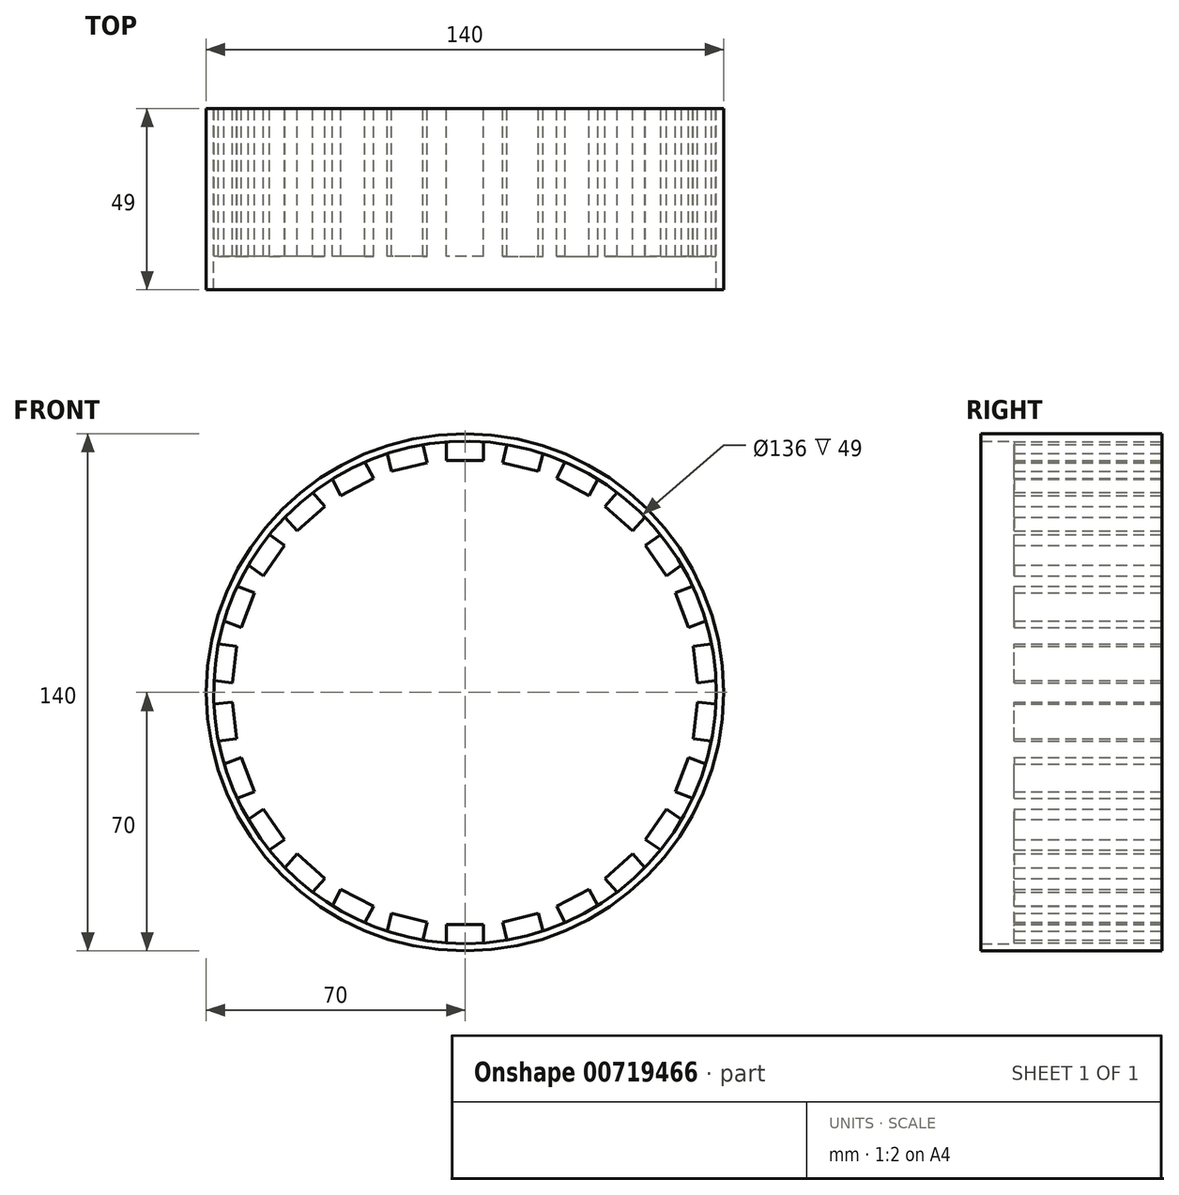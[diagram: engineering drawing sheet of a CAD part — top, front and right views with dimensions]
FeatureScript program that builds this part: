
annotation { "Feature Type Name" : "Feature", "Feature Type Description" : "" }
export const myFeature = defineFeature(function(context is Context, id is Id, definition is map)
    precondition{}
    {
        {
            var Q0;
            Q0=qCreatedBy(makeId("Front.planeOp"),FACE);
            var sketch = newSketch(context, id + "F0", { "sketchPlane" : qUnion([Q0])});
            skCircle(sketch, "E0", {"center": v(0, 0) * mm, "radius": 68 * mm});
            skCircle(sketch, "E1", {"center": v(0, 0) * mm, "radius": 70 * mm});
            skLineSegment(sketch, "E2", {"start": v(5, 67.82) * mm, "end": v(5, 62.82) * mm});
            skLineSegment(sketch, "E3", {"start": v(5, 62.82) * mm, "end": v(-5, 62.82) * mm});
            skLineSegment(sketch, "E4", {"start": v(-5, 62.82) * mm, "end": v(-5, 67.82) * mm});
            skSolve(sketch);
        }
        {
            var Q0;
            {var subQ0=sQuery(id+"F0.wireOp",EDGE,"E2");Q0=makeQuery(id+"F0.imprint","IMPRINT",FACE,{"disambiguationData":[TD([[makeQuery(id+"F0.imprint","IMPRINT",EDGE,{"derivedFrom":subQ0}),-1.0]])]});}
            var Q1;
            Q1=makeQuery(id+"F0.imprint","IMPRINT",FACE,{"disambiguationData":[TD([[makeQuery(id+"F0.imprint","IMPRINT",EDGE,{"derivedFrom":sQuery(id+"F0.wireOp",EDGE,"E1")}),1.0]])]});
            extrude(context, id + "F1", {"entities" : qUnion([Q0, Q1]), "depth" : 40 * mm, "offsetDistance" : 25 * mm});
        }
        {
            var Q0;
            Q0=makeQuery(id+"F1.opExtrude","SWEPT_BODY",BODY,{"disambiguationData":[OSD([sQuery(id+"F0.wireOp",EDGE,"E0"),sQuery(id+"F0.wireOp",EDGE,"E1"),sQuery(id+"F0.wireOp",EDGE,"E2"),sQuery(id+"F0.wireOp",EDGE,"E3"),sQuery(id+"F0.wireOp",EDGE,"E4")])]});
            var Q1;
            Q1=makeQuery(id+"F1.opExtrude","SWEPT_FACE",FACE,{"disambiguationData":[OSD([sQuery(id+"F0.wireOp",EDGE,"E0")])]});
            circularPattern(context, id + "F2", {"entities" : qUnion([Q0]), "axis" : qUnion([Q1]), "angle" : 360 * degree, "instanceCount" : 26, "equalSpace" : true});
        }
        {
            var Q0;
            Q0=makeQuery(id+"F2.opPattern","COPY",BODY,{"derivedFrom":makeQuery(id+"F1.opExtrude","SWEPT_BODY",BODY,{"disambiguationData":[OSD([sQuery(id+"F0.wireOp",EDGE,"E0"),sQuery(id+"F0.wireOp",EDGE,"E1"),sQuery(id+"F0.wireOp",EDGE,"E2"),sQuery(id+"F0.wireOp",EDGE,"E3"),sQuery(id+"F0.wireOp",EDGE,"E4")])]}),"instanceName":"3"});
            var Q1;
            Q1=makeQuery(id+"F2.opPattern","COPY",BODY,{"derivedFrom":makeQuery(id+"F1.opExtrude","SWEPT_BODY",BODY,{"disambiguationData":[OSD([sQuery(id+"F0.wireOp",EDGE,"E0"),sQuery(id+"F0.wireOp",EDGE,"E1"),sQuery(id+"F0.wireOp",EDGE,"E2"),sQuery(id+"F0.wireOp",EDGE,"E3"),sQuery(id+"F0.wireOp",EDGE,"E4")])]}),"instanceName":"4"});
            var Q2;
            Q2=makeQuery(id+"F2.opPattern","COPY",BODY,{"derivedFrom":makeQuery(id+"F1.opExtrude","SWEPT_BODY",BODY,{"disambiguationData":[OSD([sQuery(id+"F0.wireOp",EDGE,"E0"),sQuery(id+"F0.wireOp",EDGE,"E1"),sQuery(id+"F0.wireOp",EDGE,"E2"),sQuery(id+"F0.wireOp",EDGE,"E3"),sQuery(id+"F0.wireOp",EDGE,"E4")])]}),"instanceName":"6"});
            var Q3;
            Q3=makeQuery(id+"F2.opPattern","COPY",BODY,{"derivedFrom":makeQuery(id+"F1.opExtrude","SWEPT_BODY",BODY,{"disambiguationData":[OSD([sQuery(id+"F0.wireOp",EDGE,"E0"),sQuery(id+"F0.wireOp",EDGE,"E1"),sQuery(id+"F0.wireOp",EDGE,"E2"),sQuery(id+"F0.wireOp",EDGE,"E3"),sQuery(id+"F0.wireOp",EDGE,"E4")])]}),"instanceName":"10"});
            var Q4;
            Q4=makeQuery(id+"F2.opPattern","COPY",BODY,{"derivedFrom":makeQuery(id+"F1.opExtrude","SWEPT_BODY",BODY,{"disambiguationData":[OSD([sQuery(id+"F0.wireOp",EDGE,"E0"),sQuery(id+"F0.wireOp",EDGE,"E1"),sQuery(id+"F0.wireOp",EDGE,"E2"),sQuery(id+"F0.wireOp",EDGE,"E3"),sQuery(id+"F0.wireOp",EDGE,"E4")])]}),"instanceName":"8"});
            var Q5;
            Q5=makeQuery(id+"F2.opPattern","COPY",BODY,{"derivedFrom":makeQuery(id+"F1.opExtrude","SWEPT_BODY",BODY,{"disambiguationData":[OSD([sQuery(id+"F0.wireOp",EDGE,"E0"),sQuery(id+"F0.wireOp",EDGE,"E1"),sQuery(id+"F0.wireOp",EDGE,"E2"),sQuery(id+"F0.wireOp",EDGE,"E3"),sQuery(id+"F0.wireOp",EDGE,"E4")])]}),"instanceName":"11"});
            var Q6;
            Q6=makeQuery(id+"F2.opPattern","COPY",BODY,{"derivedFrom":makeQuery(id+"F1.opExtrude","SWEPT_BODY",BODY,{"disambiguationData":[OSD([sQuery(id+"F0.wireOp",EDGE,"E0"),sQuery(id+"F0.wireOp",EDGE,"E1"),sQuery(id+"F0.wireOp",EDGE,"E2"),sQuery(id+"F0.wireOp",EDGE,"E3"),sQuery(id+"F0.wireOp",EDGE,"E4")])]}),"instanceName":"12"});
            var Q7;
            Q7=makeQuery(id+"F2.opPattern","COPY",BODY,{"derivedFrom":makeQuery(id+"F1.opExtrude","SWEPT_BODY",BODY,{"disambiguationData":[OSD([sQuery(id+"F0.wireOp",EDGE,"E0"),sQuery(id+"F0.wireOp",EDGE,"E1"),sQuery(id+"F0.wireOp",EDGE,"E2"),sQuery(id+"F0.wireOp",EDGE,"E3"),sQuery(id+"F0.wireOp",EDGE,"E4")])]}),"instanceName":"9"});
            var Q8;
            Q8=makeQuery(id+"F2.opPattern","COPY",BODY,{"derivedFrom":makeQuery(id+"F1.opExtrude","SWEPT_BODY",BODY,{"disambiguationData":[OSD([sQuery(id+"F0.wireOp",EDGE,"E0"),sQuery(id+"F0.wireOp",EDGE,"E1"),sQuery(id+"F0.wireOp",EDGE,"E2"),sQuery(id+"F0.wireOp",EDGE,"E3"),sQuery(id+"F0.wireOp",EDGE,"E4")])]}),"instanceName":"2"});
            var Q9;
            Q9=makeQuery(id+"F2.opPattern","COPY",BODY,{"derivedFrom":makeQuery(id+"F1.opExtrude","SWEPT_BODY",BODY,{"disambiguationData":[OSD([sQuery(id+"F0.wireOp",EDGE,"E0"),sQuery(id+"F0.wireOp",EDGE,"E1"),sQuery(id+"F0.wireOp",EDGE,"E2"),sQuery(id+"F0.wireOp",EDGE,"E3"),sQuery(id+"F0.wireOp",EDGE,"E4")])]}),"instanceName":"15"});
            var Q10;
            Q10=makeQuery(id+"F2.opPattern","COPY",BODY,{"derivedFrom":makeQuery(id+"F1.opExtrude","SWEPT_BODY",BODY,{"disambiguationData":[OSD([sQuery(id+"F0.wireOp",EDGE,"E0"),sQuery(id+"F0.wireOp",EDGE,"E1"),sQuery(id+"F0.wireOp",EDGE,"E2"),sQuery(id+"F0.wireOp",EDGE,"E3"),sQuery(id+"F0.wireOp",EDGE,"E4")])]}),"instanceName":"13"});
            var Q11;
            Q11=makeQuery(id+"F2.opPattern","COPY",BODY,{"derivedFrom":makeQuery(id+"F1.opExtrude","SWEPT_BODY",BODY,{"disambiguationData":[OSD([sQuery(id+"F0.wireOp",EDGE,"E0"),sQuery(id+"F0.wireOp",EDGE,"E1"),sQuery(id+"F0.wireOp",EDGE,"E2"),sQuery(id+"F0.wireOp",EDGE,"E3"),sQuery(id+"F0.wireOp",EDGE,"E4")])]}),"instanceName":"16"});
            var Q12;
            Q12=makeQuery(id+"F2.opPattern","COPY",BODY,{"derivedFrom":makeQuery(id+"F1.opExtrude","SWEPT_BODY",BODY,{"disambiguationData":[OSD([sQuery(id+"F0.wireOp",EDGE,"E0"),sQuery(id+"F0.wireOp",EDGE,"E1"),sQuery(id+"F0.wireOp",EDGE,"E2"),sQuery(id+"F0.wireOp",EDGE,"E3"),sQuery(id+"F0.wireOp",EDGE,"E4")])]}),"instanceName":"14"});
            var Q13;
            Q13=makeQuery(id+"F2.opPattern","COPY",BODY,{"derivedFrom":makeQuery(id+"F1.opExtrude","SWEPT_BODY",BODY,{"disambiguationData":[OSD([sQuery(id+"F0.wireOp",EDGE,"E0"),sQuery(id+"F0.wireOp",EDGE,"E1"),sQuery(id+"F0.wireOp",EDGE,"E2"),sQuery(id+"F0.wireOp",EDGE,"E3"),sQuery(id+"F0.wireOp",EDGE,"E4")])]}),"instanceName":"19"});
            var Q14;
            Q14=makeQuery(id+"F2.opPattern","COPY",BODY,{"derivedFrom":makeQuery(id+"F1.opExtrude","SWEPT_BODY",BODY,{"disambiguationData":[OSD([sQuery(id+"F0.wireOp",EDGE,"E0"),sQuery(id+"F0.wireOp",EDGE,"E1"),sQuery(id+"F0.wireOp",EDGE,"E2"),sQuery(id+"F0.wireOp",EDGE,"E3"),sQuery(id+"F0.wireOp",EDGE,"E4")])]}),"instanceName":"18"});
            var Q15;
            Q15=makeQuery(id+"F2.opPattern","COPY",BODY,{"derivedFrom":makeQuery(id+"F1.opExtrude","SWEPT_BODY",BODY,{"disambiguationData":[OSD([sQuery(id+"F0.wireOp",EDGE,"E0"),sQuery(id+"F0.wireOp",EDGE,"E1"),sQuery(id+"F0.wireOp",EDGE,"E2"),sQuery(id+"F0.wireOp",EDGE,"E3"),sQuery(id+"F0.wireOp",EDGE,"E4")])]}),"instanceName":"17"});
            var Q16;
            Q16=makeQuery(id+"F2.opPattern","COPY",BODY,{"derivedFrom":makeQuery(id+"F1.opExtrude","SWEPT_BODY",BODY,{"disambiguationData":[OSD([sQuery(id+"F0.wireOp",EDGE,"E0"),sQuery(id+"F0.wireOp",EDGE,"E1"),sQuery(id+"F0.wireOp",EDGE,"E2"),sQuery(id+"F0.wireOp",EDGE,"E3"),sQuery(id+"F0.wireOp",EDGE,"E4")])]}),"instanceName":"7"});
            var Q17;
            Q17=makeQuery(id+"F2.opPattern","COPY",BODY,{"derivedFrom":makeQuery(id+"F1.opExtrude","SWEPT_BODY",BODY,{"disambiguationData":[OSD([sQuery(id+"F0.wireOp",EDGE,"E0"),sQuery(id+"F0.wireOp",EDGE,"E1"),sQuery(id+"F0.wireOp",EDGE,"E2"),sQuery(id+"F0.wireOp",EDGE,"E3"),sQuery(id+"F0.wireOp",EDGE,"E4")])]}),"instanceName":"23"});
            var Q18;
            Q18=makeQuery(id+"F2.opPattern","COPY",BODY,{"derivedFrom":makeQuery(id+"F1.opExtrude","SWEPT_BODY",BODY,{"disambiguationData":[OSD([sQuery(id+"F0.wireOp",EDGE,"E0"),sQuery(id+"F0.wireOp",EDGE,"E1"),sQuery(id+"F0.wireOp",EDGE,"E2"),sQuery(id+"F0.wireOp",EDGE,"E3"),sQuery(id+"F0.wireOp",EDGE,"E4")])]}),"instanceName":"22"});
            var Q19;
            Q19=makeQuery(id+"F2.opPattern","COPY",BODY,{"derivedFrom":makeQuery(id+"F1.opExtrude","SWEPT_BODY",BODY,{"disambiguationData":[OSD([sQuery(id+"F0.wireOp",EDGE,"E0"),sQuery(id+"F0.wireOp",EDGE,"E1"),sQuery(id+"F0.wireOp",EDGE,"E2"),sQuery(id+"F0.wireOp",EDGE,"E3"),sQuery(id+"F0.wireOp",EDGE,"E4")])]}),"instanceName":"21"});
            var Q20;
            Q20=makeQuery(id+"F2.opPattern","COPY",BODY,{"derivedFrom":makeQuery(id+"F1.opExtrude","SWEPT_BODY",BODY,{"disambiguationData":[OSD([sQuery(id+"F0.wireOp",EDGE,"E0"),sQuery(id+"F0.wireOp",EDGE,"E1"),sQuery(id+"F0.wireOp",EDGE,"E2"),sQuery(id+"F0.wireOp",EDGE,"E3"),sQuery(id+"F0.wireOp",EDGE,"E4")])]}),"instanceName":"20"});
            var Q21;
            Q21=makeQuery(id+"F2.opPattern","COPY",BODY,{"derivedFrom":makeQuery(id+"F1.opExtrude","SWEPT_BODY",BODY,{"disambiguationData":[OSD([sQuery(id+"F0.wireOp",EDGE,"E0"),sQuery(id+"F0.wireOp",EDGE,"E1"),sQuery(id+"F0.wireOp",EDGE,"E2"),sQuery(id+"F0.wireOp",EDGE,"E3"),sQuery(id+"F0.wireOp",EDGE,"E4")])]}),"instanceName":"24"});
            var Q22;
            Q22=makeQuery(id+"F2.opPattern","COPY",BODY,{"derivedFrom":makeQuery(id+"F1.opExtrude","SWEPT_BODY",BODY,{"disambiguationData":[OSD([sQuery(id+"F0.wireOp",EDGE,"E0"),sQuery(id+"F0.wireOp",EDGE,"E1"),sQuery(id+"F0.wireOp",EDGE,"E2"),sQuery(id+"F0.wireOp",EDGE,"E3"),sQuery(id+"F0.wireOp",EDGE,"E4")])]}),"instanceName":"1"});
            var Q23;
            Q23=makeQuery(id+"F1.opExtrude","SWEPT_BODY",BODY,{"disambiguationData":[OSD([sQuery(id+"F0.wireOp",EDGE,"E0"),sQuery(id+"F0.wireOp",EDGE,"E1"),sQuery(id+"F0.wireOp",EDGE,"E2"),sQuery(id+"F0.wireOp",EDGE,"E3"),sQuery(id+"F0.wireOp",EDGE,"E4")])]});
            var Q24;
            Q24=makeQuery(id+"F2.opPattern","COPY",BODY,{"derivedFrom":makeQuery(id+"F1.opExtrude","SWEPT_BODY",BODY,{"disambiguationData":[OSD([sQuery(id+"F0.wireOp",EDGE,"E0"),sQuery(id+"F0.wireOp",EDGE,"E1"),sQuery(id+"F0.wireOp",EDGE,"E2"),sQuery(id+"F0.wireOp",EDGE,"E3"),sQuery(id+"F0.wireOp",EDGE,"E4")])]}),"instanceName":"25"});
            var Q25;
            Q25=makeQuery(id+"F2.opPattern","COPY",BODY,{"derivedFrom":makeQuery(id+"F1.opExtrude","SWEPT_BODY",BODY,{"disambiguationData":[OSD([sQuery(id+"F0.wireOp",EDGE,"E0"),sQuery(id+"F0.wireOp",EDGE,"E1"),sQuery(id+"F0.wireOp",EDGE,"E2"),sQuery(id+"F0.wireOp",EDGE,"E3"),sQuery(id+"F0.wireOp",EDGE,"E4")])]}),"instanceName":"5"});
            booleanBodies(context, id + "F3", {"operationType" : BooleanOperationType.UNION, "tools" : qUnion([Q0, Q1, Q2, Q3, Q4, Q5, Q6, Q7, Q8, Q9, Q10, Q11, Q12, Q13, Q14, Q15, Q16, Q17, Q18, Q19, Q20, Q21, Q22, Q23, Q24, Q25])});
        }
        {
            var Q0;
            {var subQ0=makeQuery(id+"F1.opExtrude","CAP_FACE",FACE,{"disambiguationData":[OSD([sQuery(id+"F0.wireOp",EDGE,"E0"),sQuery(id+"F0.wireOp",EDGE,"E1"),sQuery(id+"F0.wireOp",EDGE,"E2"),sQuery(id+"F0.wireOp",EDGE,"E3"),sQuery(id+"F0.wireOp",EDGE,"E4")])],"isStart":false});Q0=makeQuery(id+"F3.opBoolean","MERGE",FACE,{"derivedFrom":[subQ0,makeQuery(id+"F2.opPattern","COPY",FACE,{"derivedFrom":subQ0,"instanceName":"1"}),makeQuery(id+"F2.opPattern","COPY",FACE,{"derivedFrom":subQ0,"instanceName":"2"}),makeQuery(id+"F2.opPattern","COPY",FACE,{"derivedFrom":subQ0,"instanceName":"3"}),makeQuery(id+"F2.opPattern","COPY",FACE,{"derivedFrom":subQ0,"instanceName":"4"}),makeQuery(id+"F2.opPattern","COPY",FACE,{"derivedFrom":subQ0,"instanceName":"5"}),makeQuery(id+"F2.opPattern","COPY",FACE,{"derivedFrom":subQ0,"instanceName":"6"}),makeQuery(id+"F2.opPattern","COPY",FACE,{"derivedFrom":subQ0,"instanceName":"7"}),makeQuery(id+"F2.opPattern","COPY",FACE,{"derivedFrom":subQ0,"instanceName":"8"}),makeQuery(id+"F2.opPattern","COPY",FACE,{"derivedFrom":subQ0,"instanceName":"9"}),makeQuery(id+"F2.opPattern","COPY",FACE,{"derivedFrom":subQ0,"instanceName":"10"}),makeQuery(id+"F2.opPattern","COPY",FACE,{"derivedFrom":subQ0,"instanceName":"11"}),makeQuery(id+"F2.opPattern","COPY",FACE,{"derivedFrom":subQ0,"instanceName":"12"}),makeQuery(id+"F2.opPattern","COPY",FACE,{"derivedFrom":subQ0,"instanceName":"13"}),makeQuery(id+"F2.opPattern","COPY",FACE,{"derivedFrom":subQ0,"instanceName":"14"}),makeQuery(id+"F2.opPattern","COPY",FACE,{"derivedFrom":subQ0,"instanceName":"15"}),makeQuery(id+"F2.opPattern","COPY",FACE,{"derivedFrom":subQ0,"instanceName":"16"}),makeQuery(id+"F2.opPattern","COPY",FACE,{"derivedFrom":subQ0,"instanceName":"17"}),makeQuery(id+"F2.opPattern","COPY",FACE,{"derivedFrom":subQ0,"instanceName":"18"}),makeQuery(id+"F2.opPattern","COPY",FACE,{"derivedFrom":subQ0,"instanceName":"19"}),makeQuery(id+"F2.opPattern","COPY",FACE,{"derivedFrom":subQ0,"instanceName":"20"}),makeQuery(id+"F2.opPattern","COPY",FACE,{"derivedFrom":subQ0,"instanceName":"21"}),makeQuery(id+"F2.opPattern","COPY",FACE,{"derivedFrom":subQ0,"instanceName":"22"}),makeQuery(id+"F2.opPattern","COPY",FACE,{"derivedFrom":subQ0,"instanceName":"23"}),makeQuery(id+"F2.opPattern","COPY",FACE,{"derivedFrom":subQ0,"instanceName":"24"}),makeQuery(id+"F2.opPattern","COPY",FACE,{"derivedFrom":subQ0,"instanceName":"25"})]});}
            var sketch = newSketch(context, id + "F4", { "sketchPlane" : qUnion([Q0])});
            skCircle(sketch, "E5", {"center": v(0, 0) * mm, "radius": 70 * mm});
            skCircle(sketch, "E6", {"center": v(0, 0) * mm, "radius": 68 * mm});
            skSolve(sketch);
        }
        {
            var Q0;
            Q0 = qSketchRegion(id + "F4", true);
            extrude(context, id + "F5", {"entities" : qUnion([Q0]), "operationType" : NewBodyOperationType.ADD, "depth" : 9 * mm, "offsetDistance" : 25 * mm});
        }
    });
